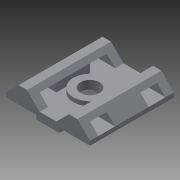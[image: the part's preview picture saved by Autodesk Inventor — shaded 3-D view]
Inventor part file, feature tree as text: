
AUTODESK INVENTOR PART (.ipt)
format: ipt  version: 2015 SP1 (Build 190203100, 203)  size: 195,072 bytes
history: native  units: mm
features: chamfer x6, sketch x6, extrude x5, hole x1
ambient origin geometry x8: Origin, YZ Plane, XZ Plane, XY Plane, X Axis, Y Axis, Z Axis, Center Point
bodies: Solid1 (feature_tree)
feature tree (18):
  extrude  "Extrusion1"  Depth=20.0mm
  extrude  "Extrusion2"  Depth=5.5mm
  extrude  "Extrusion3"  Depth=5.5mm
  extrude  "Extrusion4"  Depth=1.0mm TaperAngle=0.0deg
  hole  "Hole1"  [1 undecoded]
  extrude  "Extrusion6"  Depth=4.0mm
  chamfer  "Chamfer1"  Distance=2.0mm
  chamfer  "Chamfer2"  Distance=4.0mm
  chamfer  "Chamfer3"  Distance=4.0mm
  chamfer  "Chamfer4"  Distance=1.0mm
  chamfer  "Chamfer5"  Distance=8.0mm
  chamfer  "Chamfer6"  Distance=2.0mm
  sketch  "Sketch1"  dims[d0=20.0mm d1=20.0mm]
  sketch  "Sketch2"  dims[d3=4.0mm d4=0.0mm d5=5.5mm]
  sketch  "Sketch3"  dims[d6=1.0mm d7=0.0mm d8=5.5mm]
  sketch  "Sketch4"  dims[d9=5.5mm d10=1.0mm d11=0.0mm]
  sketch  "Sketch6"  dims[d19=1.0mm d20=0.0mm]
  sketch  "Sketch7"  dims[d24=4.5mm d25=6.0mm d26=8.0mm d27=2.0mm d28=90.0deg d29=8.0mm d30=20.594885mm d31=2.0mm d32=4.0mm d33=2.0mm d34=4.0mm d35=4.0mm d36=1.0mm d37=8.0mm d38=2.0mm d39=2.0mm d40=1.0mm d41=0.0mm d42=2.0mm d43=2.0mm d44=22.68928mm d45=2.0mm d46=2.0mm d47=22.68928mm d48=1.0mm d49=2.0mm d50=22.68928mm d51=1.0mm d52=2.0mm d53=22.68928mm d54=2.0mm d55=2.0mm d56=22.68928mm d57=2.0mm d58=2.0mm d59=22.68928mm]
note: 1 required parameter value undecoded (feature->parameter linkage not recoverable at this tier; creation-order binding heuristic only, values carry confidence <= 0.55)
